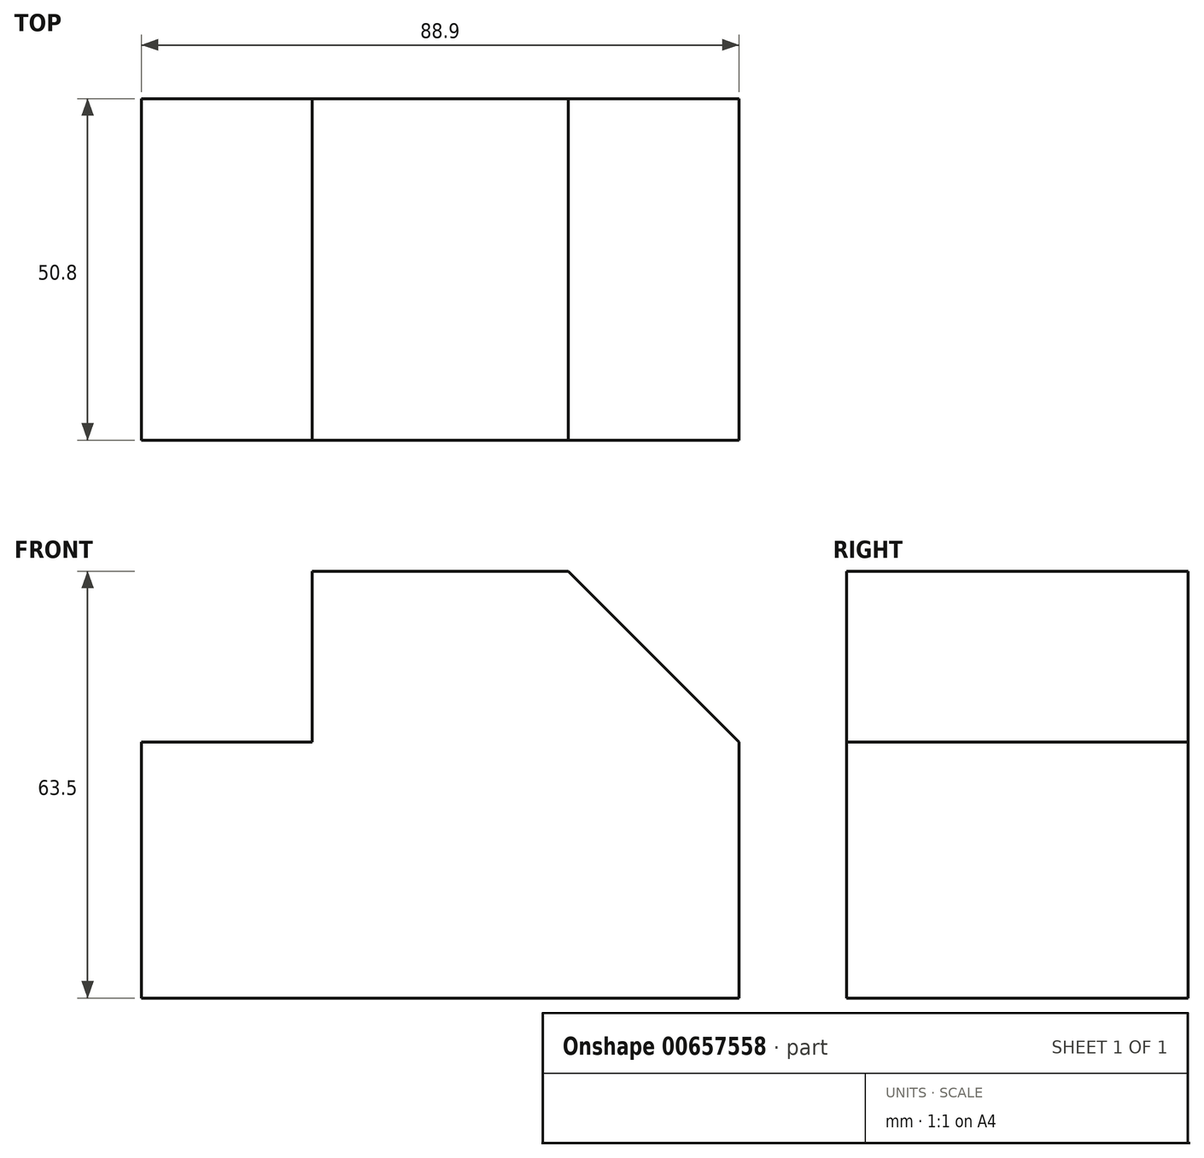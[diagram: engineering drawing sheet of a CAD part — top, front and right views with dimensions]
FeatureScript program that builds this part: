
annotation { "Feature Type Name" : "Feature", "Feature Type Description" : "" }
export const myFeature = defineFeature(function(context is Context, id is Id, definition is map)
    precondition{}
    {
        {
            var Q0;
            Q0=qCreatedBy(makeId("Front.planeOp"),FACE);
            var sketch = newSketch(context, id + "F0", { "sketchPlane" : qUnion([Q0])});
            skLineSegment(sketch, "E0", {"start": v(-47.91, -38.1) * mm, "end": v(40.99, -38.1) * mm});
            skLineSegment(sketch, "E1", {"start": v(40.99, -38.1) * mm, "end": v(40.99, 0) * mm});
            skLineSegment(sketch, "E2", {"start": v(-47.91, -38.1) * mm, "end": v(-47.91, 0) * mm});
            skLineSegment(sketch, "E3", {"start": v(-47.91, 0) * mm, "end": v(-22.51, 0) * mm});
            skLineSegment(sketch, "E4", {"start": v(-22.51, 0) * mm, "end": v(-22.51, 25.4) * mm});
            skLineSegment(sketch, "E5", {"start": v(-22.51, 25.4) * mm, "end": v(15.59, 25.4) * mm});
            skLineSegment(sketch, "E6", {"start": v(15.59, 25.4) * mm, "end": v(40.99, 0) * mm});
            skSolve(sketch);
        }
        {
            var Q0;
            Q0 = qSketchRegion(id + "F0", true);
            extrude(context, id + "F1", {"entities" : qUnion([Q0]), "depth" : 25.4 * mm, "offsetDistance" : 25.4 * mm});
        }
        {
            var Q0;
            Q0=makeQuery(id+"F1.opExtrude","CAP_FACE",FACE,{"disambiguationData":[OSD([sQuery(id+"F0.wireOp",EDGE,"E0"),sQuery(id+"F0.wireOp",EDGE,"E1"),sQuery(id+"F0.wireOp",EDGE,"E2"),sQuery(id+"F0.wireOp",EDGE,"E3"),sQuery(id+"F0.wireOp",EDGE,"E4"),sQuery(id+"F0.wireOp",EDGE,"E5"),sQuery(id+"F0.wireOp",EDGE,"E6")])],"isStart":false});
            extrude(context, id + "F2", {"entities" : qUnion([Q0]), "operationType" : NewBodyOperationType.ADD, "depth" : 25.4 * mm, "offsetDistance" : 25.4 * mm});
        }
    });
